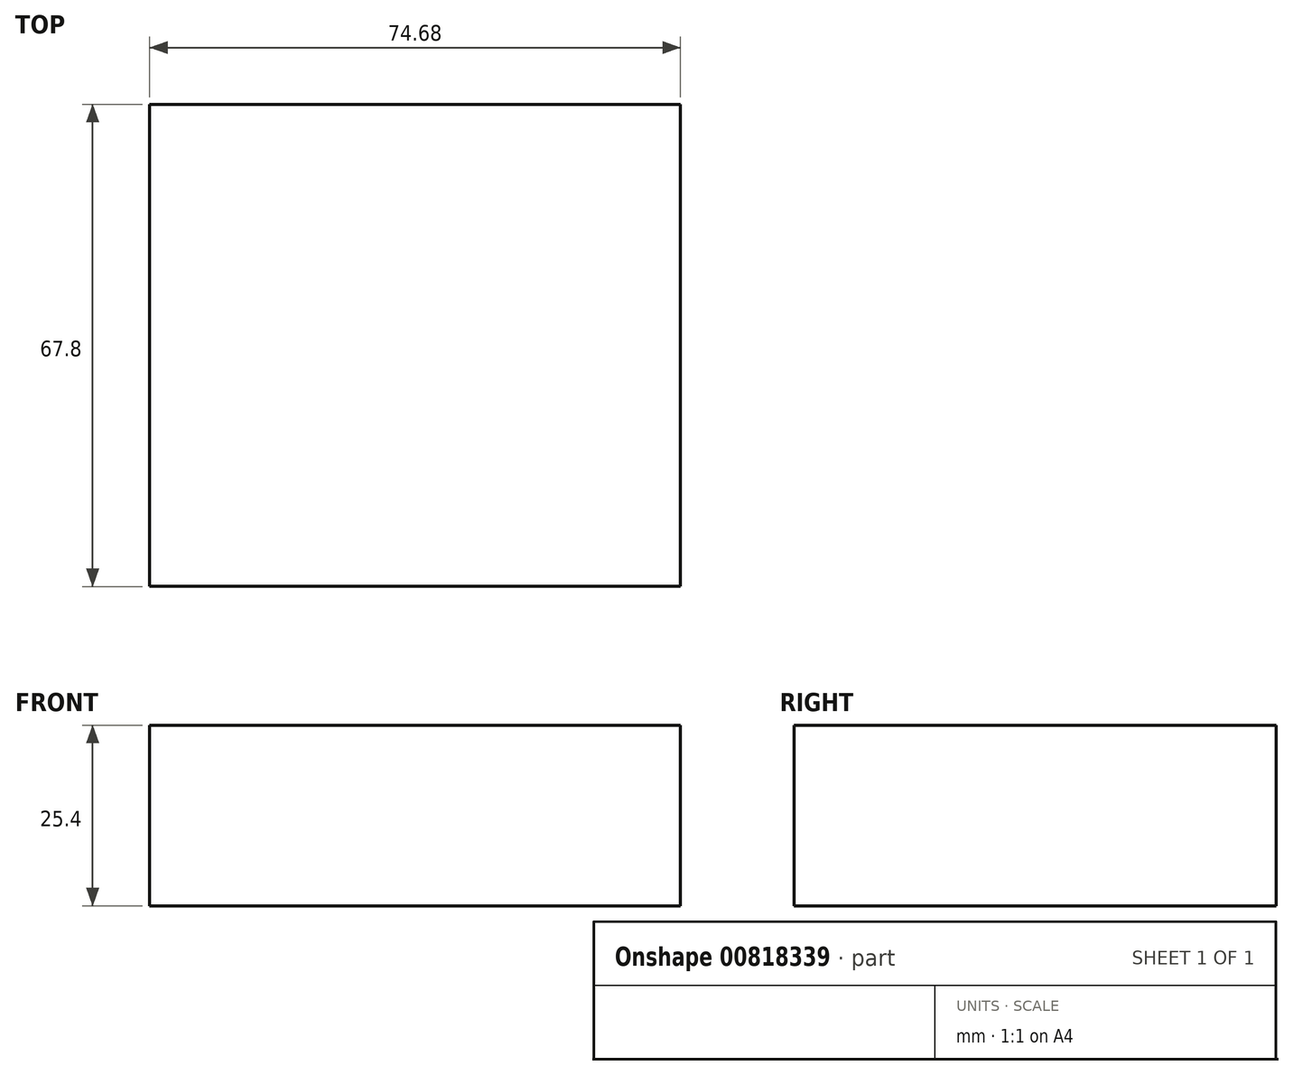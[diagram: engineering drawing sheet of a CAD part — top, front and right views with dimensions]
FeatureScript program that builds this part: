
annotation { "Feature Type Name" : "Feature", "Feature Type Description" : "" }
export const myFeature = defineFeature(function(context is Context, id is Id, definition is map)
    precondition{}
    {
        {
            var Q0;
            Q0=qCreatedBy(makeId("Top.planeOp"),FACE);
            var sketch = newSketch(context, id + "F0", { "sketchPlane" : qUnion([Q0])});
            skLineSegment(sketch, "E0.bottom", {"start": v(37.34, 33.9) * mm, "end": v(-37.34, 33.9) * mm});
            skLineSegment(sketch, "E0.top", {"start": v(37.34, -33.9) * mm, "end": v(-37.34, -33.9) * mm});
            skLineSegment(sketch, "E0.left", {"start": v(37.34, 33.9) * mm, "end": v(37.34, -33.9) * mm});
            skLineSegment(sketch, "E0.right", {"start": v(-37.34, 33.9) * mm, "end": v(-37.34, -33.9) * mm});
            skPoint(sketch, "E0.middle", {"position": v(0, 0) * mm});
            skSolve(sketch);
        }
        {
            var Q0;
            Q0 = qSketchRegion(id + "F0", true);
            extrude(context, id + "F1", {"entities" : qUnion([Q0]), "depth" : 25.4 * mm, "offsetDistance" : 25.4 * mm});
        }
    });
